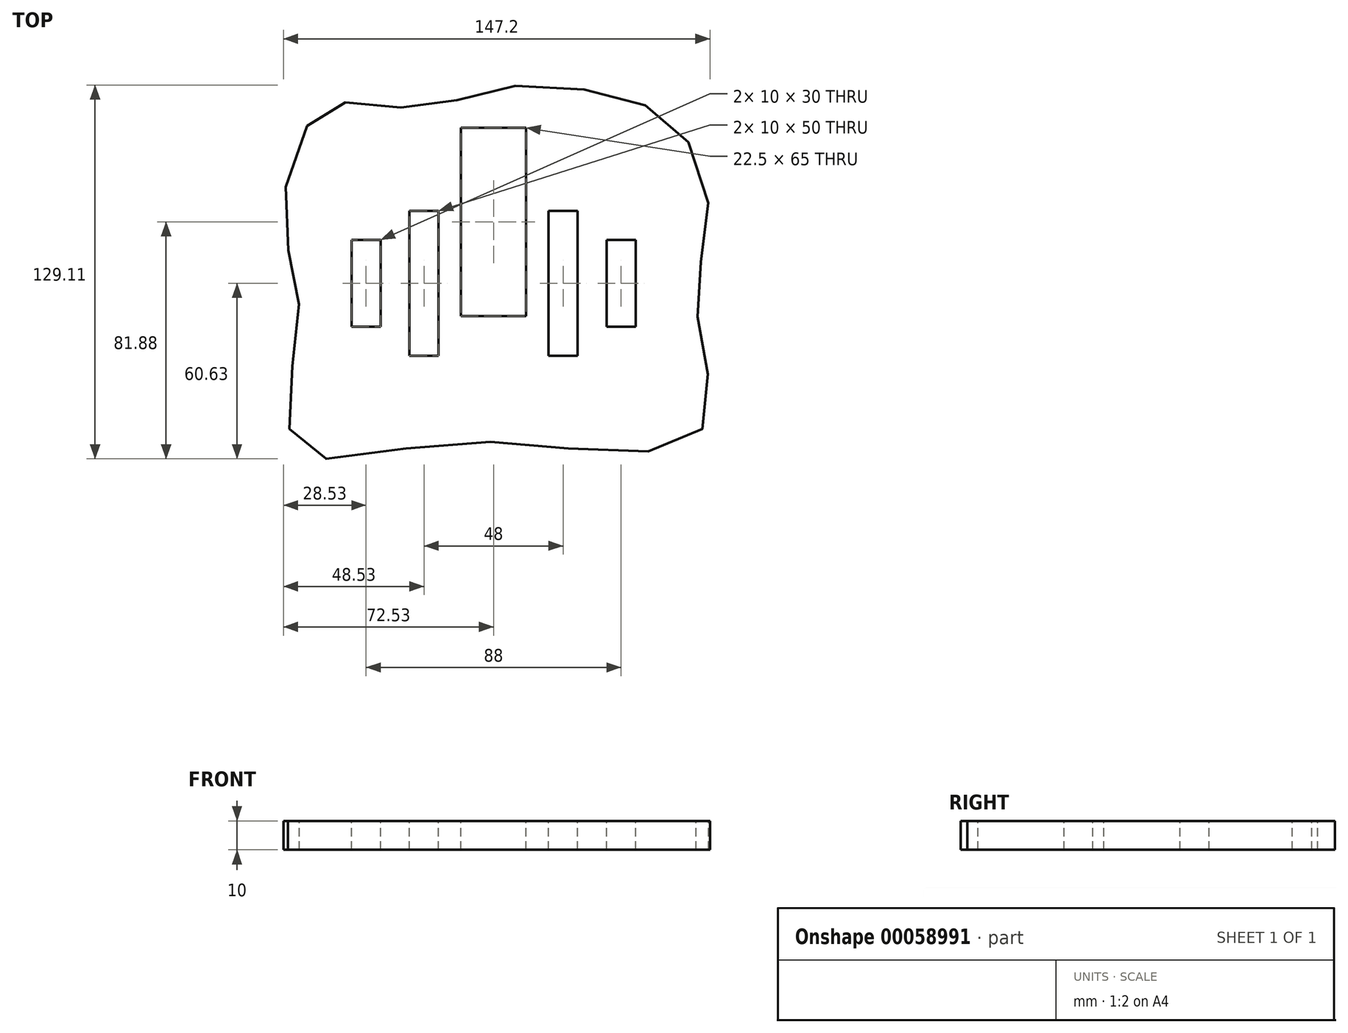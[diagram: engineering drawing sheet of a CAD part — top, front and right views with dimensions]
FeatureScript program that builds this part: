
annotation { "Feature Type Name" : "Feature", "Feature Type Description" : "" }
export const myFeature = defineFeature(function(context is Context, id is Id, definition is map)
    precondition{}
    {
        {
            var Q0;
            Q0=qCreatedBy(makeId("Top.planeOp"),FACE);
            var sketch = newSketch(context, id + "F0", { "sketchPlane" : qUnion([Q0])});
            skLineSegment(sketch, "E0.bottom", {"start": v(-62.5, 50) * mm, "end": v(62.5, 50) * mm});
            skLineSegment(sketch, "E0.top", {"start": v(-62.5, -50) * mm, "end": v(62.5, -50) * mm});
            skLineSegment(sketch, "E0.left", {"start": v(-62.5, 50) * mm, "end": v(-62.5, -50) * mm});
            skLineSegment(sketch, "E0.right", {"start": v(62.5, 50) * mm, "end": v(62.5, -50) * mm});
            skPoint(sketch, "E0.middle", {"position": v(0, 0) * mm});
            skSolve(sketch);
        }
        {
            var Q0;
            Q0 = qSketchRegion(id + "F0", true);
            extrude(context, id + "F1", {"entities" : qUnion([Q0]), "depth" : 10 * mm});
        }
        {
            var Q0;
            Q0=makeQuery(id+"F1.opExtrude","CAP_FACE",FACE,{"disambiguationData":[OSD([sQuery(id+"F0.wireOp",EDGE,"E0.bottom"),sQuery(id+"F0.wireOp",EDGE,"E0.top"),sQuery(id+"F0.wireOp",EDGE,"E0.left"),sQuery(id+"F0.wireOp",EDGE,"E0.right")])],"isStart":false});
            var sketch = newSketch(context, id + "F2", { "sketchPlane" : qUnion([Q0])});
            skLineSegment(sketch, "E1.bottom", {"start": v(-19, 25) * mm, "end": v(-29, 25) * mm});
            skLineSegment(sketch, "E1.top", {"start": v(-19, -25) * mm, "end": v(-29, -25) * mm});
            skLineSegment(sketch, "E1.left", {"start": v(-19, 25) * mm, "end": v(-19, -25) * mm});
            skLineSegment(sketch, "E1.right", {"start": v(-29, 25) * mm, "end": v(-29, -25) * mm});
            skPoint(sketch, "E1.middle", {"position": v(-24, 0) * mm});
            skPoint(sketch, "E2.MirrorP", {"position": v(24, 0) * mm});
            skLineSegment(sketch, "E3.MirrorCS", {"start": v(19, 25) * mm, "end": v(29, 25) * mm});
            skLineSegment(sketch, "E4.MirrorCS", {"start": v(19, -25) * mm, "end": v(29, -25) * mm});
            skLineSegment(sketch, "E5.MirrorCS", {"start": v(29, 25) * mm, "end": v(29, -25) * mm});
            skLineSegment(sketch, "E6.MirrorCS", {"start": v(19, 25) * mm, "end": v(19, -25) * mm});
            skSolve(sketch);
        }
        {
            var Q0;
            Q0 = qSketchRegion(id + "F2", true);
            extrude(context, id + "F3", {"entities" : qUnion([Q0]), "operationType" : NewBodyOperationType.REMOVE, "oppositeDirection" : true, "depth" : 25 * mm});
        }
        {
            var Q0;
            Q0=makeQuery(id+"F1.opExtrude","CAP_FACE",FACE,{"disambiguationData":[OSD([sQuery(id+"F0.wireOp",EDGE,"E0.bottom"),sQuery(id+"F0.wireOp",EDGE,"E0.top"),sQuery(id+"F0.wireOp",EDGE,"E0.left"),sQuery(id+"F0.wireOp",EDGE,"E0.right")])],"isStart":false});
            var sketch = newSketch(context, id + "F4", { "sketchPlane" : qUnion([Q0])});
            skLineSegment(sketch, "E7.bottom", {"start": v(-39, 15) * mm, "end": v(-49, 15) * mm});
            skLineSegment(sketch, "E7.top", {"start": v(-39, -15) * mm, "end": v(-49, -15) * mm});
            skLineSegment(sketch, "E7.left", {"start": v(-39, 15) * mm, "end": v(-39, -15) * mm});
            skLineSegment(sketch, "E7.right", {"start": v(-49, 15) * mm, "end": v(-49, -15) * mm});
            skPoint(sketch, "E7.middle", {"position": v(-44, 0) * mm});
            skLineSegment(sketch, "E8.MirrorCS", {"start": v(49, 15) * mm, "end": v(49, -15) * mm});
            skLineSegment(sketch, "E9.MirrorCS", {"start": v(39, 15) * mm, "end": v(39, -15) * mm});
            skLineSegment(sketch, "E10.MirrorCS", {"start": v(39, -15) * mm, "end": v(49, -15) * mm});
            skLineSegment(sketch, "E11.MirrorCS", {"start": v(39, 15) * mm, "end": v(49, 15) * mm});
            skPoint(sketch, "E12.MirrorP", {"position": v(44, 0) * mm});
            skSolve(sketch);
        }
        {
            var Q0;
            Q0 = qSketchRegion(id + "F4", true);
            extrude(context, id + "F5", {"entities" : qUnion([Q0]), "operationType" : NewBodyOperationType.REMOVE, "oppositeDirection" : true, "depth" : 25 * mm});
        }
        {
            var Q0;
            Q0=makeQuery(id+"F1.opExtrude","CAP_FACE",FACE,{"disambiguationData":[OSD([sQuery(id+"F0.wireOp",EDGE,"E0.bottom"),sQuery(id+"F0.wireOp",EDGE,"E0.top"),sQuery(id+"F0.wireOp",EDGE,"E0.left"),sQuery(id+"F0.wireOp",EDGE,"E0.right")])],"isStart":false});
            var sketch = newSketch(context, id + "F6", { "sketchPlane" : qUnion([Q0])});
            skFitSpline(sketch, "E13", {"points": [v(-64.3, 54.38) * mm, v(-50.29, 62.52) * mm, v(-24.22, 60.54) * mm, v(1.94, 67.51) * mm, v(38.98, 65.46) * mm, v(63.42, 53.73) * mm, v(74.17, 24.4) * mm, v(69.94, -2.64) * mm, v(73.52, -28.38) * mm, v(70.59, -52.16) * mm, v(32.8, -57.7) * mm, v(-19.01, -55.42) * mm, v(-65.28, -58.68) * mm, v(-70.49, -36.2) * mm, v(-67.23, -4.6) * mm, v(-72.44, 20.82) * mm, v(-64.3, 54.38) * mm]});
            skLineSegment(sketch, "E14.bottom", {"start": v(-62.5, 50) * mm, "end": v(62.5, 50) * mm});
            skLineSegment(sketch, "E14.top", {"start": v(-62.5, -50) * mm, "end": v(62.5, -50) * mm});
            skLineSegment(sketch, "E14.left", {"start": v(-62.5, 50) * mm, "end": v(-62.5, -50) * mm});
            skLineSegment(sketch, "E14.right", {"start": v(62.5, 50) * mm, "end": v(62.5, -50) * mm});
            skPoint(sketch, "E14.middle", {"position": v(0, 0) * mm});
            skSolve(sketch);
        }
        {
            var Q0;
            Q0 = qSketchRegion(id + "F6", true);
            extrude(context, id + "F7", {"entities" : qUnion([Q0]), "operationType" : NewBodyOperationType.ADD, "oppositeDirection" : true, "depth" : 10 * mm});
        }
        {
            var Q0;
            Q0=makeQuery(id+"F1.opExtrude","CAP_FACE",FACE,{"disambiguationData":[OSD([sQuery(id+"F0.wireOp",EDGE,"E0.bottom"),sQuery(id+"F0.wireOp",EDGE,"E0.top"),sQuery(id+"F0.wireOp",EDGE,"E0.left"),sQuery(id+"F0.wireOp",EDGE,"E0.right")])],"isStart":false});
            var sketch = newSketch(context, id + "F8", { "sketchPlane" : qUnion([Q0])});
            skLineSegment(sketch, "E15.bottom", {"start": v(11.25, -11.25) * mm, "end": v(-11.25, -11.25) * mm});
            skLineSegment(sketch, "E15.top", {"start": v(11.25, 53.75) * mm, "end": v(-11.25, 53.75) * mm});
            skLineSegment(sketch, "E15.left", {"start": v(11.25, -11.25) * mm, "end": v(11.25, 53.75) * mm});
            skLineSegment(sketch, "E15.right", {"start": v(-11.25, -11.25) * mm, "end": v(-11.25, 53.75) * mm});
            skPoint(sketch, "E15.middle", {"position": v(0, 21.25) * mm});
            skSolve(sketch);
        }
        {
            var Q0;
            Q0 = qSketchRegion(id + "F8", true);
            extrude(context, id + "F9", {"entities" : qUnion([Q0]), "operationType" : NewBodyOperationType.REMOVE, "oppositeDirection" : true, "depth" : 25 * mm});
        }
    });
